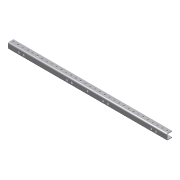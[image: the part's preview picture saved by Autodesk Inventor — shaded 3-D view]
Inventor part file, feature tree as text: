
AUTODESK INVENTOR PART (.ipt)
format: ipt  version: 2013 (Build 170138000, 138)  size: 226,304 bytes
history: native  units: in
note: dims shown in document units (in); Inventor stores cm internally (conversion verified against a paired STEP export)
features: projected_geometry x8, extrude x2, sketch x2, other x1, imported_body x1
ambient origin geometry x8: Origin, YZ Plane, XZ Plane, XY Plane, X Axis, Y Axis, Z Axis, Center Point
feature tree (14):
  other  "Short C Channel for drive1"
  extrude  "Extrusion1"  TaperAngle=0.0deg  [1 undecoded]
  extrude  "Extrusion2"  [1 undecoded]
  imported_body  "Base1"
  sketch  "Sketch1"  dims[d1=0.0in d3=0.0in]
  projected_geometry  "Projected Loop1"
  projected_geometry  "Projected Loop2"
  projected_geometry  "Projected Loop3"
  projected_geometry  "Projected Loop4"
  sketch  "Sketch2"
  projected_geometry  "Projected Loop5"
  projected_geometry  "Projected Loop6"
  projected_geometry  "Projected Loop7"
  projected_geometry  "Projected Loop8"
note: 2 required parameter values undecoded (feature->parameter linkage not recoverable at this tier; creation-order binding heuristic only, values carry confidence <= 0.55)
